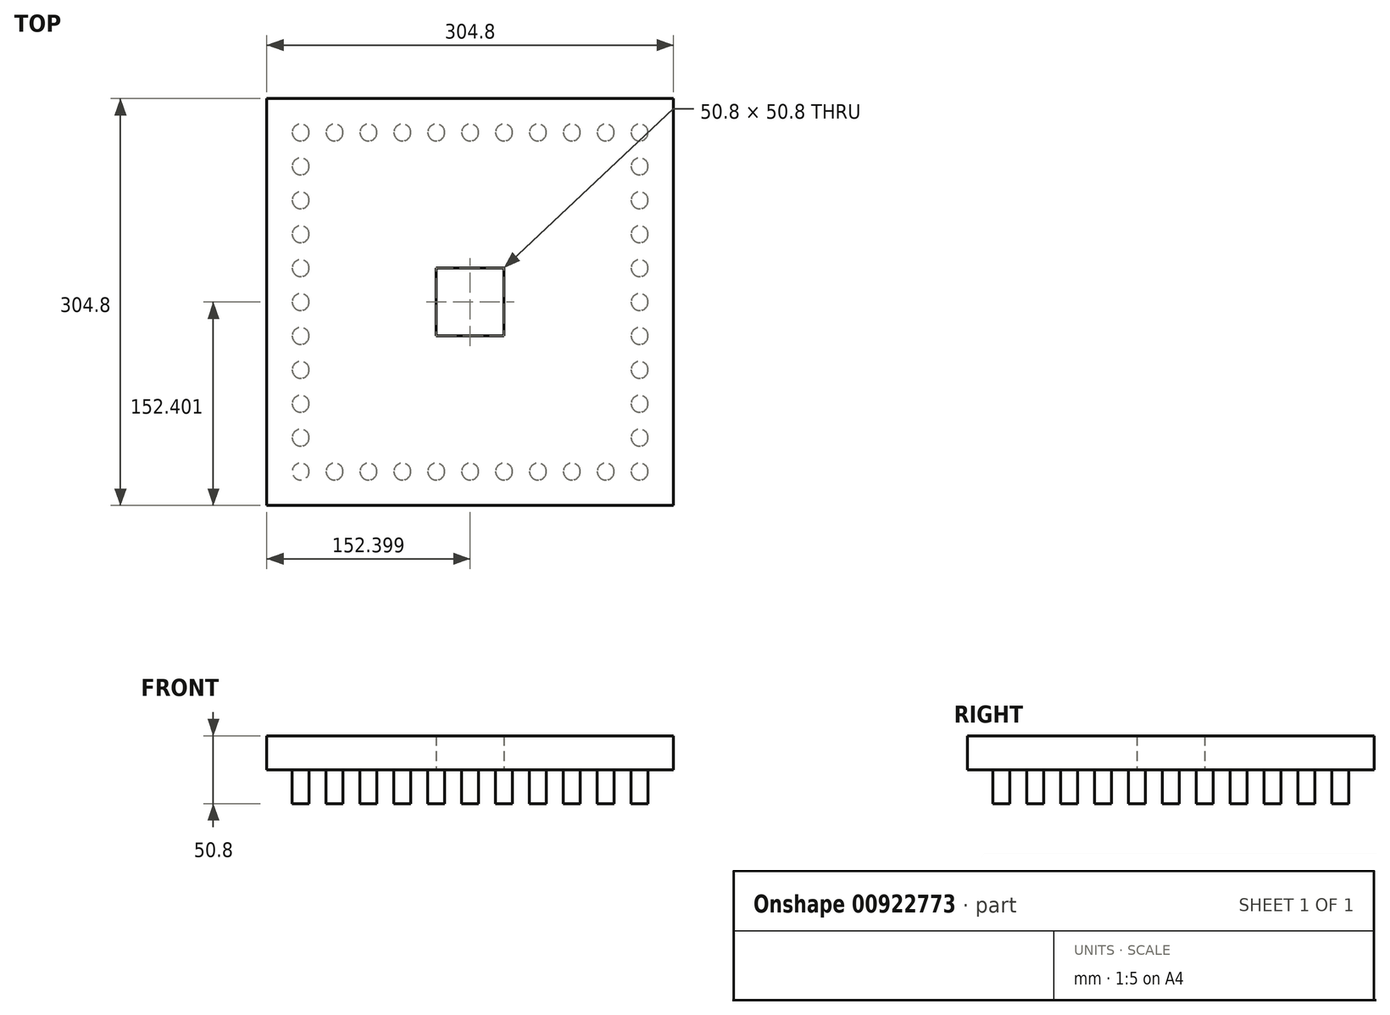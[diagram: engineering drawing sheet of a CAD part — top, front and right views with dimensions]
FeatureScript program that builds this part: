
annotation { "Feature Type Name" : "Feature", "Feature Type Description" : "" }
export const myFeature = defineFeature(function(context is Context, id is Id, definition is map)
    precondition{}
    {
        {
            var Q0;
            Q0=qCreatedBy(makeId("Top.planeOp"),FACE);
            var sketch = newSketch(context, id + "F0", { "sketchPlane" : qUnion([Q0])});
            skLineSegment(sketch, "E0.bottom", {"start": v(-170.88, 244.81) * mm, "end": v(133.92, 244.81) * mm});
            skLineSegment(sketch, "E0.top", {"start": v(-170.88, -59.99) * mm, "end": v(133.92, -59.99) * mm});
            skLineSegment(sketch, "E0.left", {"start": v(-170.88, 244.81) * mm, "end": v(-170.88, -59.99) * mm});
            skLineSegment(sketch, "E0.right", {"start": v(133.92, 244.81) * mm, "end": v(133.92, -59.99) * mm});
            skSolve(sketch);
        }
        {
            var Q0;
            Q0=makeQuery(id+"F0.imprint","IMPRINT",FACE,{"disambiguationData":[TD([[makeQuery(id+"F0.imprint","IMPRINT",EDGE,{"derivedFrom":sQuery(id+"F0.wireOp",EDGE,"E0.bottom")}),-1.0]])]});
            extrude(context, id + "F1", {"entities" : qUnion([Q0]), "depth" : 25.4 * mm, "offsetDistance" : 25.4 * mm});
        }
        {
            var Q0;
            Q0=makeQuery(id+"F1.opExtrude","CAP_FACE",FACE,{"disambiguationData":[OSD([sQuery(id+"F0.wireOp",EDGE,"E0.bottom"),sQuery(id+"F0.wireOp",EDGE,"E0.top"),sQuery(id+"F0.wireOp",EDGE,"E0.left"),sQuery(id+"F0.wireOp",EDGE,"E0.right")])],"isStart":true});
            var sketch = newSketch(context, id + "F2", { "sketchPlane" : qUnion([Q0])});
            skLineSegment(sketch, "E1", {"start": v(-170.88, 59.99) * mm, "end": v(-145.48, 59.99) * mm});
            skLineSegment(sketch, "E2", {"start": v(-145.48, 59.99) * mm, "end": v(-145.48, 34.59) * mm});
            skLineSegment(sketch, "E3", {"start": v(-145.48, 34.59) * mm, "end": v(-145.48, 9.19) * mm});
            skLineSegment(sketch, "E4", {"start": v(-145.48, 9.19) * mm, "end": v(-145.48, -16.21) * mm});
            skLineSegment(sketch, "E5", {"start": v(-145.48, -16.21) * mm, "end": v(-145.48, -41.61) * mm});
            skLineSegment(sketch, "E6", {"start": v(-145.48, -41.61) * mm, "end": v(-145.48, -67.01) * mm});
            skLineSegment(sketch, "E7", {"start": v(-145.48, -67.01) * mm, "end": v(-145.48, -92.41) * mm});
            skLineSegment(sketch, "E8", {"start": v(-145.48, -92.41) * mm, "end": v(-145.48, -117.81) * mm});
            skLineSegment(sketch, "E9", {"start": v(-145.48, -117.81) * mm, "end": v(-145.48, -117.81) * mm});
            skLineSegment(sketch, "E10", {"start": v(-145.48, -117.81) * mm, "end": v(-145.48, -143.21) * mm});
            skLineSegment(sketch, "E11", {"start": v(-145.48, -143.21) * mm, "end": v(-145.48, -168.61) * mm});
            skLineSegment(sketch, "E12", {"start": v(-145.48, -168.61) * mm, "end": v(-145.48, -194.01) * mm});
            skLineSegment(sketch, "E13", {"start": v(-145.48, -194.01) * mm, "end": v(-145.48, -219.41) * mm});
            skLineSegment(sketch, "E14", {"start": v(-145.48, -219.41) * mm, "end": v(-145.48, -244.81) * mm});
            skLineSegment(sketch, "E15", {"start": v(-145.48, -219.41) * mm, "end": v(-120.08, -219.41) * mm});
            skLineSegment(sketch, "E16", {"start": v(-120.08, -219.41) * mm, "end": v(-94.68, -219.41) * mm});
            skLineSegment(sketch, "E17", {"start": v(-94.68, -219.41) * mm, "end": v(-69.28, -219.41) * mm});
            skLineSegment(sketch, "E18", {"start": v(-69.28, -219.41) * mm, "end": v(-43.88, -219.41) * mm});
            skLineSegment(sketch, "E19", {"start": v(-43.88, -219.41) * mm, "end": v(-18.48, -219.41) * mm});
            skLineSegment(sketch, "E20", {"start": v(-18.48, -219.41) * mm, "end": v(6.92, -219.41) * mm});
            skLineSegment(sketch, "E21", {"start": v(6.92, -219.41) * mm, "end": v(32.32, -219.41) * mm});
            skLineSegment(sketch, "E22", {"start": v(32.32, -219.41) * mm, "end": v(57.72, -219.41) * mm});
            skLineSegment(sketch, "E23", {"start": v(57.72, -219.41) * mm, "end": v(83.12, -219.41) * mm});
            skLineSegment(sketch, "E24", {"start": v(83.12, -219.41) * mm, "end": v(108.52, -219.41) * mm});
            skLineSegment(sketch, "E25", {"start": v(108.52, -219.41) * mm, "end": v(108.52, -194.01) * mm});
            skLineSegment(sketch, "E26", {"start": v(108.52, -194.01) * mm, "end": v(108.52, -168.61) * mm});
            skLineSegment(sketch, "E27", {"start": v(108.52, -168.61) * mm, "end": v(108.52, -143.21) * mm});
            skLineSegment(sketch, "E28", {"start": v(108.52, -143.21) * mm, "end": v(108.52, -117.81) * mm});
            skLineSegment(sketch, "E29", {"start": v(108.52, -117.81) * mm, "end": v(108.52, -92.41) * mm});
            skLineSegment(sketch, "E30", {"start": v(108.52, -92.41) * mm, "end": v(108.52, -67.01) * mm});
            skLineSegment(sketch, "E31", {"start": v(108.52, -67.01) * mm, "end": v(108.52, -41.61) * mm});
            skLineSegment(sketch, "E32", {"start": v(108.52, -41.61) * mm, "end": v(108.52, -16.21) * mm});
            skLineSegment(sketch, "E33", {"start": v(108.52, -16.21) * mm, "end": v(108.52, 9.19) * mm});
            skLineSegment(sketch, "E34", {"start": v(108.52, 9.19) * mm, "end": v(108.52, 34.59) * mm});
            skLineSegment(sketch, "E35", {"start": v(108.52, 34.59) * mm, "end": v(83.12, 34.59) * mm});
            skLineSegment(sketch, "E36", {"start": v(83.12, 34.59) * mm, "end": v(57.72, 34.59) * mm});
            skLineSegment(sketch, "E37", {"start": v(57.72, 34.59) * mm, "end": v(32.32, 34.59) * mm});
            skLineSegment(sketch, "E38", {"start": v(32.32, 34.59) * mm, "end": v(6.92, 34.59) * mm});
            skLineSegment(sketch, "E39", {"start": v(6.92, 34.59) * mm, "end": v(-18.48, 34.59) * mm});
            skLineSegment(sketch, "E40", {"start": v(-18.48, 34.59) * mm, "end": v(-43.88, 34.59) * mm});
            skLineSegment(sketch, "E41", {"start": v(-43.88, 34.59) * mm, "end": v(-69.28, 34.59) * mm});
            skLineSegment(sketch, "E42", {"start": v(-69.28, 34.59) * mm, "end": v(-94.68, 34.59) * mm});
            skLineSegment(sketch, "E43", {"start": v(-94.68, 34.59) * mm, "end": v(-120.08, 34.59) * mm});
            skCircle(sketch, "E44", {"center": v(-145.48, 34.59) * mm, "radius": 6.35 * mm});
            skCircle(sketch, "E45", {"center": v(-145.48, 9.19) * mm, "radius": 6.35 * mm});
            skCircle(sketch, "E46", {"center": v(-145.48, -16.21) * mm, "radius": 6.35 * mm});
            skCircle(sketch, "E47", {"center": v(-145.48, -41.61) * mm, "radius": 6.35 * mm});
            skCircle(sketch, "E48", {"center": v(-145.48, -67.01) * mm, "radius": 6.35 * mm});
            skCircle(sketch, "E49", {"center": v(-145.48, -92.41) * mm, "radius": 6.35 * mm});
            skCircle(sketch, "E50", {"center": v(-145.48, -117.81) * mm, "radius": 6.35 * mm});
            skCircle(sketch, "E51", {"center": v(-145.48, -143.21) * mm, "radius": 6.35 * mm});
            skCircle(sketch, "E52", {"center": v(-145.48, -168.61) * mm, "radius": 6.35 * mm});
            skCircle(sketch, "E53", {"center": v(-145.48, -194.01) * mm, "radius": 6.35 * mm});
            skCircle(sketch, "E54", {"center": v(-145.48, -219.41) * mm, "radius": 6.35 * mm});
            skCircle(sketch, "E55", {"center": v(-120.08, -219.41) * mm, "radius": 6.35 * mm});
            skCircle(sketch, "E56", {"center": v(-94.68, -219.41) * mm, "radius": 6.35 * mm});
            skCircle(sketch, "E57", {"center": v(-69.28, -219.41) * mm, "radius": 6.35 * mm});
            skCircle(sketch, "E58", {"center": v(-43.88, -219.41) * mm, "radius": 6.35 * mm});
            skCircle(sketch, "E59", {"center": v(-18.48, -219.41) * mm, "radius": 6.35 * mm});
            skCircle(sketch, "E60", {"center": v(6.92, -219.41) * mm, "radius": 6.35 * mm});
            skCircle(sketch, "E61", {"center": v(32.32, -219.41) * mm, "radius": 6.35 * mm});
            skCircle(sketch, "E62", {"center": v(57.72, -219.41) * mm, "radius": 6.35 * mm});
            skCircle(sketch, "E63", {"center": v(83.12, -219.41) * mm, "radius": 6.35 * mm});
            skCircle(sketch, "E64", {"center": v(108.52, -219.41) * mm, "radius": 6.35 * mm});
            skCircle(sketch, "E65", {"center": v(108.52, -194.01) * mm, "radius": 6.35 * mm});
            skCircle(sketch, "E66", {"center": v(108.52, -168.61) * mm, "radius": 6.35 * mm});
            skCircle(sketch, "E67", {"center": v(108.52, -143.21) * mm, "radius": 6.35 * mm});
            skCircle(sketch, "E68", {"center": v(108.52, -117.81) * mm, "radius": 6.35 * mm});
            skCircle(sketch, "E69", {"center": v(108.52, -92.41) * mm, "radius": 6.35 * mm});
            skCircle(sketch, "E70", {"center": v(108.52, -67.01) * mm, "radius": 6.35 * mm});
            skCircle(sketch, "E71", {"center": v(108.52, -41.61) * mm, "radius": 6.35 * mm});
            skCircle(sketch, "E72", {"center": v(108.52, -16.21) * mm, "radius": 6.35 * mm});
            skCircle(sketch, "E73", {"center": v(108.52, 9.19) * mm, "radius": 6.35 * mm});
            skCircle(sketch, "E74", {"center": v(108.52, 34.59) * mm, "radius": 6.35 * mm});
            skCircle(sketch, "E75", {"center": v(-120.08, 34.59) * mm, "radius": 6.35 * mm});
            skCircle(sketch, "E76", {"center": v(-94.68, 34.59) * mm, "radius": 6.35 * mm});
            skCircle(sketch, "E77", {"center": v(-69.28, 34.59) * mm, "radius": 6.35 * mm});
            skCircle(sketch, "E78", {"center": v(-43.88, 34.59) * mm, "radius": 6.35 * mm});
            skCircle(sketch, "E79", {"center": v(-18.48, 34.59) * mm, "radius": 6.35 * mm});
            skCircle(sketch, "E80", {"center": v(6.92, 34.59) * mm, "radius": 6.35 * mm});
            skCircle(sketch, "E81", {"center": v(32.32, 34.59) * mm, "radius": 6.35 * mm});
            skCircle(sketch, "E82", {"center": v(57.72, 34.59) * mm, "radius": 6.35 * mm});
            skCircle(sketch, "E83", {"center": v(83.12, 34.59) * mm, "radius": 6.35 * mm});
            skSolve(sketch);
        }
        {
            var Q0;
            {var subQ0=sQuery(id+"F2.wireOp",EDGE,"E3");var subQ1=sQuery(id+"F2.wireOp",EDGE,"E2");var subQ2=makeQuery(id+"F2.imprint","INTERSECT",VERTEX,{"derivedFrom":[subQ1,subQ0]});Q0=makeQuery(id+"F2.imprint","IMPRINT",FACE,{"disambiguationData":[TD([[makeQuery(id+"F2.imprint","IMPRINT",EDGE,{"disambiguationData":[TD([[subQ2,1.0]])],"derivedFrom":subQ1}),-1.0]])]});}
            var Q1;
            {var subQ0=sQuery(id+"F2.wireOp",EDGE,"E4");var subQ1=sQuery(id+"F2.wireOp",EDGE,"E3");var subQ2=makeQuery(id+"F2.imprint","INTERSECT",VERTEX,{"derivedFrom":[subQ1,subQ0]});Q1=makeQuery(id+"F2.imprint","IMPRINT",FACE,{"disambiguationData":[TD([[makeQuery(id+"F2.imprint","IMPRINT",EDGE,{"disambiguationData":[TD([[subQ2,1.0]])],"derivedFrom":subQ1}),-1.0]])]});}
            var Q2;
            {var subQ0=sQuery(id+"F2.wireOp",EDGE,"E4");var subQ1=sQuery(id+"F2.wireOp",EDGE,"E3");var subQ2=makeQuery(id+"F2.imprint","INTERSECT",VERTEX,{"derivedFrom":[subQ1,subQ0]});Q2=makeQuery(id+"F2.imprint","IMPRINT",FACE,{"disambiguationData":[TD([[makeQuery(id+"F2.imprint","IMPRINT",EDGE,{"disambiguationData":[TD([[subQ2,1.0]])],"derivedFrom":subQ1}),1.0]])]});}
            var Q3;
            {var subQ0=sQuery(id+"F2.wireOp",EDGE,"E3");var subQ1=sQuery(id+"F2.wireOp",EDGE,"E2");var subQ2=makeQuery(id+"F2.imprint","INTERSECT",VERTEX,{"derivedFrom":[subQ1,subQ0]});Q3=makeQuery(id+"F2.imprint","IMPRINT",FACE,{"disambiguationData":[TD([[makeQuery(id+"F2.imprint","IMPRINT",EDGE,{"disambiguationData":[TD([[subQ2,1.0]])],"derivedFrom":subQ1}),1.0]])]});}
            var Q4;
            {var subQ0=sQuery(id+"F2.wireOp",EDGE,"E5");var subQ1=sQuery(id+"F2.wireOp",EDGE,"E4");var subQ2=makeQuery(id+"F2.imprint","INTERSECT",VERTEX,{"derivedFrom":[subQ1,subQ0]});Q4=makeQuery(id+"F2.imprint","IMPRINT",FACE,{"disambiguationData":[TD([[makeQuery(id+"F2.imprint","IMPRINT",EDGE,{"disambiguationData":[TD([[subQ2,1.0]])],"derivedFrom":subQ1}),-1.0]])]});}
            var Q5;
            {var subQ0=sQuery(id+"F2.wireOp",EDGE,"E5");var subQ1=sQuery(id+"F2.wireOp",EDGE,"E4");var subQ2=makeQuery(id+"F2.imprint","INTERSECT",VERTEX,{"derivedFrom":[subQ1,subQ0]});Q5=makeQuery(id+"F2.imprint","IMPRINT",FACE,{"disambiguationData":[TD([[makeQuery(id+"F2.imprint","IMPRINT",EDGE,{"disambiguationData":[TD([[subQ2,1.0]])],"derivedFrom":subQ1}),1.0]])]});}
            var Q6;
            {var subQ0=sQuery(id+"F2.wireOp",EDGE,"E6");var subQ1=sQuery(id+"F2.wireOp",EDGE,"E5");var subQ2=makeQuery(id+"F2.imprint","INTERSECT",VERTEX,{"derivedFrom":[subQ1,subQ0]});Q6=makeQuery(id+"F2.imprint","IMPRINT",FACE,{"disambiguationData":[TD([[makeQuery(id+"F2.imprint","IMPRINT",EDGE,{"disambiguationData":[TD([[subQ2,1.0]])],"derivedFrom":subQ1}),-1.0]])]});}
            var Q7;
            {var subQ0=sQuery(id+"F2.wireOp",EDGE,"E6");var subQ1=sQuery(id+"F2.wireOp",EDGE,"E5");var subQ2=makeQuery(id+"F2.imprint","INTERSECT",VERTEX,{"derivedFrom":[subQ1,subQ0]});Q7=makeQuery(id+"F2.imprint","IMPRINT",FACE,{"disambiguationData":[TD([[makeQuery(id+"F2.imprint","IMPRINT",EDGE,{"disambiguationData":[TD([[subQ2,1.0]])],"derivedFrom":subQ1}),1.0]])]});}
            var Q8;
            {var subQ0=sQuery(id+"F2.wireOp",EDGE,"E7");var subQ1=sQuery(id+"F2.wireOp",EDGE,"E6");var subQ2=makeQuery(id+"F2.imprint","INTERSECT",VERTEX,{"derivedFrom":[subQ1,subQ0]});Q8=makeQuery(id+"F2.imprint","IMPRINT",FACE,{"disambiguationData":[TD([[makeQuery(id+"F2.imprint","IMPRINT",EDGE,{"disambiguationData":[TD([[subQ2,1.0]])],"derivedFrom":subQ1}),-1.0]])]});}
            var Q9;
            {var subQ0=sQuery(id+"F2.wireOp",EDGE,"E7");var subQ1=sQuery(id+"F2.wireOp",EDGE,"E6");var subQ2=makeQuery(id+"F2.imprint","INTERSECT",VERTEX,{"derivedFrom":[subQ1,subQ0]});Q9=makeQuery(id+"F2.imprint","IMPRINT",FACE,{"disambiguationData":[TD([[makeQuery(id+"F2.imprint","IMPRINT",EDGE,{"disambiguationData":[TD([[subQ2,1.0]])],"derivedFrom":subQ1}),1.0]])]});}
            var Q10;
            {var subQ0=sQuery(id+"F2.wireOp",EDGE,"E8");var subQ1=sQuery(id+"F2.wireOp",EDGE,"E7");var subQ2=makeQuery(id+"F2.imprint","INTERSECT",VERTEX,{"derivedFrom":[subQ1,subQ0]});Q10=makeQuery(id+"F2.imprint","IMPRINT",FACE,{"disambiguationData":[TD([[makeQuery(id+"F2.imprint","IMPRINT",EDGE,{"disambiguationData":[TD([[subQ2,1.0]])],"derivedFrom":subQ1}),1.0]])]});}
            var Q11;
            {var subQ0=sQuery(id+"F2.wireOp",EDGE,"E8");var subQ1=sQuery(id+"F2.wireOp",EDGE,"E7");var subQ2=makeQuery(id+"F2.imprint","INTERSECT",VERTEX,{"derivedFrom":[subQ1,subQ0]});Q11=makeQuery(id+"F2.imprint","IMPRINT",FACE,{"disambiguationData":[TD([[makeQuery(id+"F2.imprint","IMPRINT",EDGE,{"disambiguationData":[TD([[subQ2,1.0]])],"derivedFrom":subQ1}),-1.0]])]});}
            var Q12;
            {var subQ0=sQuery(id+"F2.wireOp",EDGE,"E10");var subQ1=sQuery(id+"F2.wireOp",EDGE,"E8");var subQ2=makeQuery(id+"F2.imprint","INTERSECT",VERTEX,{"derivedFrom":[subQ1,subQ0]});Q12=makeQuery(id+"F2.imprint","IMPRINT",FACE,{"disambiguationData":[TD([[makeQuery(id+"F2.imprint","IMPRINT",EDGE,{"disambiguationData":[TD([[subQ2,1.0]])],"derivedFrom":subQ1}),1.0]])]});}
            var Q13;
            {var subQ0=sQuery(id+"F2.wireOp",EDGE,"E10");var subQ1=sQuery(id+"F2.wireOp",EDGE,"E8");var subQ2=makeQuery(id+"F2.imprint","INTERSECT",VERTEX,{"derivedFrom":[subQ1,subQ0]});Q13=makeQuery(id+"F2.imprint","IMPRINT",FACE,{"disambiguationData":[TD([[makeQuery(id+"F2.imprint","IMPRINT",EDGE,{"disambiguationData":[TD([[subQ2,1.0]])],"derivedFrom":subQ1}),-1.0]])]});}
            var Q14;
            {var subQ0=sQuery(id+"F2.wireOp",EDGE,"E11");var subQ1=sQuery(id+"F2.wireOp",EDGE,"E10");var subQ2=makeQuery(id+"F2.imprint","INTERSECT",VERTEX,{"derivedFrom":[subQ1,subQ0]});Q14=makeQuery(id+"F2.imprint","IMPRINT",FACE,{"disambiguationData":[TD([[makeQuery(id+"F2.imprint","IMPRINT",EDGE,{"disambiguationData":[TD([[subQ2,1.0]])],"derivedFrom":subQ1}),-1.0]])]});}
            var Q15;
            {var subQ0=sQuery(id+"F2.wireOp",EDGE,"E11");var subQ1=sQuery(id+"F2.wireOp",EDGE,"E10");var subQ2=makeQuery(id+"F2.imprint","INTERSECT",VERTEX,{"derivedFrom":[subQ1,subQ0]});Q15=makeQuery(id+"F2.imprint","IMPRINT",FACE,{"disambiguationData":[TD([[makeQuery(id+"F2.imprint","IMPRINT",EDGE,{"disambiguationData":[TD([[subQ2,1.0]])],"derivedFrom":subQ1}),1.0]])]});}
            var Q16;
            Q16=makeQuery(id+"F2.imprint","IMPRINT",FACE,{"disambiguationData":[TD([[makeQuery(id+"F2.imprint","IMPRINT",EDGE,{"derivedFrom":sQuery(id+"F2.wireOp",EDGE,"E75")}),1.0]])]});
            var Q17;
            {var subQ0=sQuery(id+"F2.wireOp",EDGE,"E43");var subQ1=sQuery(id+"F2.wireOp",EDGE,"E42");var subQ2=makeQuery(id+"F2.imprint","INTERSECT",VERTEX,{"derivedFrom":[subQ1,subQ0]});Q17=makeQuery(id+"F2.imprint","IMPRINT",FACE,{"disambiguationData":[TD([[makeQuery(id+"F2.imprint","IMPRINT",EDGE,{"disambiguationData":[TD([[subQ2,1.0]])],"derivedFrom":subQ1}),1.0]])]});}
            var Q18;
            {var subQ0=sQuery(id+"F2.wireOp",EDGE,"E43");var subQ1=sQuery(id+"F2.wireOp",EDGE,"E42");var subQ2=makeQuery(id+"F2.imprint","INTERSECT",VERTEX,{"derivedFrom":[subQ1,subQ0]});Q18=makeQuery(id+"F2.imprint","IMPRINT",FACE,{"disambiguationData":[TD([[makeQuery(id+"F2.imprint","IMPRINT",EDGE,{"disambiguationData":[TD([[subQ2,1.0]])],"derivedFrom":subQ1}),-1.0]])]});}
            var Q19;
            {var subQ0=sQuery(id+"F2.wireOp",EDGE,"E42");var subQ1=sQuery(id+"F2.wireOp",EDGE,"E41");var subQ2=makeQuery(id+"F2.imprint","INTERSECT",VERTEX,{"derivedFrom":[subQ1,subQ0]});Q19=makeQuery(id+"F2.imprint","IMPRINT",FACE,{"disambiguationData":[TD([[makeQuery(id+"F2.imprint","IMPRINT",EDGE,{"disambiguationData":[TD([[subQ2,1.0]])],"derivedFrom":subQ1}),-1.0]])]});}
            var Q20;
            {var subQ0=sQuery(id+"F2.wireOp",EDGE,"E42");var subQ1=sQuery(id+"F2.wireOp",EDGE,"E41");var subQ2=makeQuery(id+"F2.imprint","INTERSECT",VERTEX,{"derivedFrom":[subQ1,subQ0]});Q20=makeQuery(id+"F2.imprint","IMPRINT",FACE,{"disambiguationData":[TD([[makeQuery(id+"F2.imprint","IMPRINT",EDGE,{"disambiguationData":[TD([[subQ2,1.0]])],"derivedFrom":subQ1}),1.0]])]});}
            var Q21;
            {var subQ0=sQuery(id+"F2.wireOp",EDGE,"E41");var subQ1=sQuery(id+"F2.wireOp",EDGE,"E40");var subQ2=makeQuery(id+"F2.imprint","INTERSECT",VERTEX,{"derivedFrom":[subQ1,subQ0]});Q21=makeQuery(id+"F2.imprint","IMPRINT",FACE,{"disambiguationData":[TD([[makeQuery(id+"F2.imprint","IMPRINT",EDGE,{"disambiguationData":[TD([[subQ2,1.0]])],"derivedFrom":subQ1}),-1.0]])]});}
            var Q22;
            {var subQ0=sQuery(id+"F2.wireOp",EDGE,"E41");var subQ1=sQuery(id+"F2.wireOp",EDGE,"E40");var subQ2=makeQuery(id+"F2.imprint","INTERSECT",VERTEX,{"derivedFrom":[subQ1,subQ0]});Q22=makeQuery(id+"F2.imprint","IMPRINT",FACE,{"disambiguationData":[TD([[makeQuery(id+"F2.imprint","IMPRINT",EDGE,{"disambiguationData":[TD([[subQ2,1.0]])],"derivedFrom":subQ1}),1.0]])]});}
            var Q23;
            {var subQ0=sQuery(id+"F2.wireOp",EDGE,"E40");var subQ1=sQuery(id+"F2.wireOp",EDGE,"E39");var subQ2=makeQuery(id+"F2.imprint","INTERSECT",VERTEX,{"derivedFrom":[subQ1,subQ0]});Q23=makeQuery(id+"F2.imprint","IMPRINT",FACE,{"disambiguationData":[TD([[makeQuery(id+"F2.imprint","IMPRINT",EDGE,{"disambiguationData":[TD([[subQ2,1.0]])],"derivedFrom":subQ1}),-1.0]])]});}
            var Q24;
            {var subQ0=sQuery(id+"F2.wireOp",EDGE,"E40");var subQ1=sQuery(id+"F2.wireOp",EDGE,"E39");var subQ2=makeQuery(id+"F2.imprint","INTERSECT",VERTEX,{"derivedFrom":[subQ1,subQ0]});Q24=makeQuery(id+"F2.imprint","IMPRINT",FACE,{"disambiguationData":[TD([[makeQuery(id+"F2.imprint","IMPRINT",EDGE,{"disambiguationData":[TD([[subQ2,1.0]])],"derivedFrom":subQ1}),1.0]])]});}
            var Q25;
            {var subQ0=sQuery(id+"F2.wireOp",EDGE,"E39");var subQ1=sQuery(id+"F2.wireOp",EDGE,"E38");var subQ2=makeQuery(id+"F2.imprint","INTERSECT",VERTEX,{"derivedFrom":[subQ1,subQ0]});Q25=makeQuery(id+"F2.imprint","IMPRINT",FACE,{"disambiguationData":[TD([[makeQuery(id+"F2.imprint","IMPRINT",EDGE,{"disambiguationData":[TD([[subQ2,1.0]])],"derivedFrom":subQ1}),-1.0]])]});}
            var Q26;
            {var subQ0=sQuery(id+"F2.wireOp",EDGE,"E39");var subQ1=sQuery(id+"F2.wireOp",EDGE,"E38");var subQ2=makeQuery(id+"F2.imprint","INTERSECT",VERTEX,{"derivedFrom":[subQ1,subQ0]});Q26=makeQuery(id+"F2.imprint","IMPRINT",FACE,{"disambiguationData":[TD([[makeQuery(id+"F2.imprint","IMPRINT",EDGE,{"disambiguationData":[TD([[subQ2,1.0]])],"derivedFrom":subQ1}),1.0]])]});}
            var Q27;
            {var subQ0=sQuery(id+"F2.wireOp",EDGE,"E38");var subQ1=sQuery(id+"F2.wireOp",EDGE,"E37");var subQ2=makeQuery(id+"F2.imprint","INTERSECT",VERTEX,{"derivedFrom":[subQ1,subQ0]});Q27=makeQuery(id+"F2.imprint","IMPRINT",FACE,{"disambiguationData":[TD([[makeQuery(id+"F2.imprint","IMPRINT",EDGE,{"disambiguationData":[TD([[subQ2,1.0]])],"derivedFrom":subQ1}),-1.0]])]});}
            var Q28;
            {var subQ0=sQuery(id+"F2.wireOp",EDGE,"E38");var subQ1=sQuery(id+"F2.wireOp",EDGE,"E37");var subQ2=makeQuery(id+"F2.imprint","INTERSECT",VERTEX,{"derivedFrom":[subQ1,subQ0]});Q28=makeQuery(id+"F2.imprint","IMPRINT",FACE,{"disambiguationData":[TD([[makeQuery(id+"F2.imprint","IMPRINT",EDGE,{"disambiguationData":[TD([[subQ2,1.0]])],"derivedFrom":subQ1}),1.0]])]});}
            var Q29;
            {var subQ0=sQuery(id+"F2.wireOp",EDGE,"E37");var subQ1=sQuery(id+"F2.wireOp",EDGE,"E36");var subQ2=makeQuery(id+"F2.imprint","INTERSECT",VERTEX,{"derivedFrom":[subQ1,subQ0]});Q29=makeQuery(id+"F2.imprint","IMPRINT",FACE,{"disambiguationData":[TD([[makeQuery(id+"F2.imprint","IMPRINT",EDGE,{"disambiguationData":[TD([[subQ2,1.0]])],"derivedFrom":subQ1}),-1.0]])]});}
            var Q30;
            {var subQ0=sQuery(id+"F2.wireOp",EDGE,"E37");var subQ1=sQuery(id+"F2.wireOp",EDGE,"E36");var subQ2=makeQuery(id+"F2.imprint","INTERSECT",VERTEX,{"derivedFrom":[subQ1,subQ0]});Q30=makeQuery(id+"F2.imprint","IMPRINT",FACE,{"disambiguationData":[TD([[makeQuery(id+"F2.imprint","IMPRINT",EDGE,{"disambiguationData":[TD([[subQ2,1.0]])],"derivedFrom":subQ1}),1.0]])]});}
            var Q31;
            {var subQ0=sQuery(id+"F2.wireOp",EDGE,"E36");var subQ1=sQuery(id+"F2.wireOp",EDGE,"E35");var subQ2=makeQuery(id+"F2.imprint","INTERSECT",VERTEX,{"derivedFrom":[subQ1,subQ0]});Q31=makeQuery(id+"F2.imprint","IMPRINT",FACE,{"disambiguationData":[TD([[makeQuery(id+"F2.imprint","IMPRINT",EDGE,{"disambiguationData":[TD([[subQ2,1.0]])],"derivedFrom":subQ1}),-1.0]])]});}
            var Q32;
            {var subQ0=sQuery(id+"F2.wireOp",EDGE,"E36");var subQ1=sQuery(id+"F2.wireOp",EDGE,"E35");var subQ2=makeQuery(id+"F2.imprint","INTERSECT",VERTEX,{"derivedFrom":[subQ1,subQ0]});Q32=makeQuery(id+"F2.imprint","IMPRINT",FACE,{"disambiguationData":[TD([[makeQuery(id+"F2.imprint","IMPRINT",EDGE,{"disambiguationData":[TD([[subQ2,1.0]])],"derivedFrom":subQ1}),1.0]])]});}
            var Q33;
            {var subQ0=sQuery(id+"F2.wireOp",EDGE,"E35");var subQ1=sQuery(id+"F2.wireOp",EDGE,"E34");var subQ2=makeQuery(id+"F2.imprint","INTERSECT",VERTEX,{"derivedFrom":[subQ1,subQ0]});Q33=makeQuery(id+"F2.imprint","IMPRINT",FACE,{"disambiguationData":[TD([[makeQuery(id+"F2.imprint","IMPRINT",EDGE,{"disambiguationData":[TD([[subQ2,1.0]])],"derivedFrom":subQ1}),-1.0]])]});}
            var Q34;
            {var subQ0=sQuery(id+"F2.wireOp",EDGE,"E35");var subQ1=sQuery(id+"F2.wireOp",EDGE,"E34");var subQ2=makeQuery(id+"F2.imprint","INTERSECT",VERTEX,{"derivedFrom":[subQ1,subQ0]});Q34=makeQuery(id+"F2.imprint","IMPRINT",FACE,{"disambiguationData":[TD([[makeQuery(id+"F2.imprint","IMPRINT",EDGE,{"disambiguationData":[TD([[subQ2,1.0]])],"derivedFrom":subQ1}),1.0]])]});}
            var Q35;
            {var subQ0=sQuery(id+"F2.wireOp",EDGE,"E34");var subQ1=sQuery(id+"F2.wireOp",EDGE,"E33");var subQ2=makeQuery(id+"F2.imprint","INTERSECT",VERTEX,{"derivedFrom":[subQ1,subQ0]});Q35=makeQuery(id+"F2.imprint","IMPRINT",FACE,{"disambiguationData":[TD([[makeQuery(id+"F2.imprint","IMPRINT",EDGE,{"disambiguationData":[TD([[subQ2,1.0]])],"derivedFrom":subQ1}),-1.0]])]});}
            var Q36;
            {var subQ0=sQuery(id+"F2.wireOp",EDGE,"E34");var subQ1=sQuery(id+"F2.wireOp",EDGE,"E33");var subQ2=makeQuery(id+"F2.imprint","INTERSECT",VERTEX,{"derivedFrom":[subQ1,subQ0]});Q36=makeQuery(id+"F2.imprint","IMPRINT",FACE,{"disambiguationData":[TD([[makeQuery(id+"F2.imprint","IMPRINT",EDGE,{"disambiguationData":[TD([[subQ2,1.0]])],"derivedFrom":subQ1}),1.0]])]});}
            var Q37;
            {var subQ0=sQuery(id+"F2.wireOp",EDGE,"E33");var subQ1=sQuery(id+"F2.wireOp",EDGE,"E32");var subQ2=makeQuery(id+"F2.imprint","INTERSECT",VERTEX,{"derivedFrom":[subQ1,subQ0]});Q37=makeQuery(id+"F2.imprint","IMPRINT",FACE,{"disambiguationData":[TD([[makeQuery(id+"F2.imprint","IMPRINT",EDGE,{"disambiguationData":[TD([[subQ2,1.0]])],"derivedFrom":subQ1}),-1.0]])]});}
            var Q38;
            {var subQ0=sQuery(id+"F2.wireOp",EDGE,"E33");var subQ1=sQuery(id+"F2.wireOp",EDGE,"E32");var subQ2=makeQuery(id+"F2.imprint","INTERSECT",VERTEX,{"derivedFrom":[subQ1,subQ0]});Q38=makeQuery(id+"F2.imprint","IMPRINT",FACE,{"disambiguationData":[TD([[makeQuery(id+"F2.imprint","IMPRINT",EDGE,{"disambiguationData":[TD([[subQ2,1.0]])],"derivedFrom":subQ1}),1.0]])]});}
            var Q39;
            {var subQ0=sQuery(id+"F2.wireOp",EDGE,"E32");var subQ1=sQuery(id+"F2.wireOp",EDGE,"E31");var subQ2=makeQuery(id+"F2.imprint","INTERSECT",VERTEX,{"derivedFrom":[subQ1,subQ0]});Q39=makeQuery(id+"F2.imprint","IMPRINT",FACE,{"disambiguationData":[TD([[makeQuery(id+"F2.imprint","IMPRINT",EDGE,{"disambiguationData":[TD([[subQ2,1.0]])],"derivedFrom":subQ1}),-1.0]])]});}
            var Q40;
            {var subQ0=sQuery(id+"F2.wireOp",EDGE,"E32");var subQ1=sQuery(id+"F2.wireOp",EDGE,"E31");var subQ2=makeQuery(id+"F2.imprint","INTERSECT",VERTEX,{"derivedFrom":[subQ1,subQ0]});Q40=makeQuery(id+"F2.imprint","IMPRINT",FACE,{"disambiguationData":[TD([[makeQuery(id+"F2.imprint","IMPRINT",EDGE,{"disambiguationData":[TD([[subQ2,1.0]])],"derivedFrom":subQ1}),1.0]])]});}
            var Q41;
            {var subQ0=sQuery(id+"F2.wireOp",EDGE,"E31");var subQ1=sQuery(id+"F2.wireOp",EDGE,"E30");var subQ2=makeQuery(id+"F2.imprint","INTERSECT",VERTEX,{"derivedFrom":[subQ1,subQ0]});Q41=makeQuery(id+"F2.imprint","IMPRINT",FACE,{"disambiguationData":[TD([[makeQuery(id+"F2.imprint","IMPRINT",EDGE,{"disambiguationData":[TD([[subQ2,1.0]])],"derivedFrom":subQ1}),-1.0]])]});}
            var Q42;
            {var subQ0=sQuery(id+"F2.wireOp",EDGE,"E31");var subQ1=sQuery(id+"F2.wireOp",EDGE,"E30");var subQ2=makeQuery(id+"F2.imprint","INTERSECT",VERTEX,{"derivedFrom":[subQ1,subQ0]});Q42=makeQuery(id+"F2.imprint","IMPRINT",FACE,{"disambiguationData":[TD([[makeQuery(id+"F2.imprint","IMPRINT",EDGE,{"disambiguationData":[TD([[subQ2,1.0]])],"derivedFrom":subQ1}),1.0]])]});}
            var Q43;
            {var subQ0=sQuery(id+"F2.wireOp",EDGE,"E30");var subQ1=sQuery(id+"F2.wireOp",EDGE,"E29");var subQ2=makeQuery(id+"F2.imprint","INTERSECT",VERTEX,{"derivedFrom":[subQ1,subQ0]});Q43=makeQuery(id+"F2.imprint","IMPRINT",FACE,{"disambiguationData":[TD([[makeQuery(id+"F2.imprint","IMPRINT",EDGE,{"disambiguationData":[TD([[subQ2,1.0]])],"derivedFrom":subQ1}),1.0]])]});}
            var Q44;
            {var subQ0=sQuery(id+"F2.wireOp",EDGE,"E30");var subQ1=sQuery(id+"F2.wireOp",EDGE,"E29");var subQ2=makeQuery(id+"F2.imprint","INTERSECT",VERTEX,{"derivedFrom":[subQ1,subQ0]});Q44=makeQuery(id+"F2.imprint","IMPRINT",FACE,{"disambiguationData":[TD([[makeQuery(id+"F2.imprint","IMPRINT",EDGE,{"disambiguationData":[TD([[subQ2,1.0]])],"derivedFrom":subQ1}),-1.0]])]});}
            var Q45;
            {var subQ0=sQuery(id+"F2.wireOp",EDGE,"E29");var subQ1=sQuery(id+"F2.wireOp",EDGE,"E28");var subQ2=makeQuery(id+"F2.imprint","INTERSECT",VERTEX,{"derivedFrom":[subQ1,subQ0]});Q45=makeQuery(id+"F2.imprint","IMPRINT",FACE,{"disambiguationData":[TD([[makeQuery(id+"F2.imprint","IMPRINT",EDGE,{"disambiguationData":[TD([[subQ2,1.0]])],"derivedFrom":subQ1}),-1.0]])]});}
            var Q46;
            {var subQ0=sQuery(id+"F2.wireOp",EDGE,"E29");var subQ1=sQuery(id+"F2.wireOp",EDGE,"E28");var subQ2=makeQuery(id+"F2.imprint","INTERSECT",VERTEX,{"derivedFrom":[subQ1,subQ0]});Q46=makeQuery(id+"F2.imprint","IMPRINT",FACE,{"disambiguationData":[TD([[makeQuery(id+"F2.imprint","IMPRINT",EDGE,{"disambiguationData":[TD([[subQ2,1.0]])],"derivedFrom":subQ1}),1.0]])]});}
            var Q47;
            {var subQ0=sQuery(id+"F2.wireOp",EDGE,"E28");var subQ1=sQuery(id+"F2.wireOp",EDGE,"E27");var subQ2=makeQuery(id+"F2.imprint","INTERSECT",VERTEX,{"derivedFrom":[subQ1,subQ0]});Q47=makeQuery(id+"F2.imprint","IMPRINT",FACE,{"disambiguationData":[TD([[makeQuery(id+"F2.imprint","IMPRINT",EDGE,{"disambiguationData":[TD([[subQ2,1.0]])],"derivedFrom":subQ1}),-1.0]])]});}
            var Q48;
            {var subQ0=sQuery(id+"F2.wireOp",EDGE,"E28");var subQ1=sQuery(id+"F2.wireOp",EDGE,"E27");var subQ2=makeQuery(id+"F2.imprint","INTERSECT",VERTEX,{"derivedFrom":[subQ1,subQ0]});Q48=makeQuery(id+"F2.imprint","IMPRINT",FACE,{"disambiguationData":[TD([[makeQuery(id+"F2.imprint","IMPRINT",EDGE,{"disambiguationData":[TD([[subQ2,1.0]])],"derivedFrom":subQ1}),1.0]])]});}
            var Q49;
            {var subQ0=sQuery(id+"F2.wireOp",EDGE,"E27");var subQ1=sQuery(id+"F2.wireOp",EDGE,"E26");var subQ2=makeQuery(id+"F2.imprint","INTERSECT",VERTEX,{"derivedFrom":[subQ1,subQ0]});Q49=makeQuery(id+"F2.imprint","IMPRINT",FACE,{"disambiguationData":[TD([[makeQuery(id+"F2.imprint","IMPRINT",EDGE,{"disambiguationData":[TD([[subQ2,1.0]])],"derivedFrom":subQ1}),-1.0]])]});}
            var Q50;
            {var subQ0=sQuery(id+"F2.wireOp",EDGE,"E27");var subQ1=sQuery(id+"F2.wireOp",EDGE,"E26");var subQ2=makeQuery(id+"F2.imprint","INTERSECT",VERTEX,{"derivedFrom":[subQ1,subQ0]});Q50=makeQuery(id+"F2.imprint","IMPRINT",FACE,{"disambiguationData":[TD([[makeQuery(id+"F2.imprint","IMPRINT",EDGE,{"disambiguationData":[TD([[subQ2,1.0]])],"derivedFrom":subQ1}),1.0]])]});}
            var Q51;
            {var subQ0=sQuery(id+"F2.wireOp",EDGE,"E26");var subQ1=sQuery(id+"F2.wireOp",EDGE,"E25");var subQ2=makeQuery(id+"F2.imprint","INTERSECT",VERTEX,{"derivedFrom":[subQ1,subQ0]});Q51=makeQuery(id+"F2.imprint","IMPRINT",FACE,{"disambiguationData":[TD([[makeQuery(id+"F2.imprint","IMPRINT",EDGE,{"disambiguationData":[TD([[subQ2,1.0]])],"derivedFrom":subQ1}),-1.0]])]});}
            var Q52;
            {var subQ0=sQuery(id+"F2.wireOp",EDGE,"E26");var subQ1=sQuery(id+"F2.wireOp",EDGE,"E25");var subQ2=makeQuery(id+"F2.imprint","INTERSECT",VERTEX,{"derivedFrom":[subQ1,subQ0]});Q52=makeQuery(id+"F2.imprint","IMPRINT",FACE,{"disambiguationData":[TD([[makeQuery(id+"F2.imprint","IMPRINT",EDGE,{"disambiguationData":[TD([[subQ2,1.0]])],"derivedFrom":subQ1}),1.0]])]});}
            var Q53;
            {var subQ0=sQuery(id+"F2.wireOp",EDGE,"E25");var subQ1=sQuery(id+"F2.wireOp",EDGE,"E24");var subQ2=makeQuery(id+"F2.imprint","INTERSECT",VERTEX,{"derivedFrom":[subQ1,subQ0]});Q53=makeQuery(id+"F2.imprint","IMPRINT",FACE,{"disambiguationData":[TD([[makeQuery(id+"F2.imprint","IMPRINT",EDGE,{"disambiguationData":[TD([[subQ2,1.0]])],"derivedFrom":subQ1}),-1.0]])]});}
            var Q54;
            {var subQ0=sQuery(id+"F2.wireOp",EDGE,"E25");var subQ1=sQuery(id+"F2.wireOp",EDGE,"E24");var subQ2=makeQuery(id+"F2.imprint","INTERSECT",VERTEX,{"derivedFrom":[subQ1,subQ0]});Q54=makeQuery(id+"F2.imprint","IMPRINT",FACE,{"disambiguationData":[TD([[makeQuery(id+"F2.imprint","IMPRINT",EDGE,{"disambiguationData":[TD([[subQ2,1.0]])],"derivedFrom":subQ1}),1.0]])]});}
            var Q55;
            {var subQ0=sQuery(id+"F2.wireOp",EDGE,"E24");var subQ1=sQuery(id+"F2.wireOp",EDGE,"E23");var subQ2=makeQuery(id+"F2.imprint","INTERSECT",VERTEX,{"derivedFrom":[subQ1,subQ0]});Q55=makeQuery(id+"F2.imprint","IMPRINT",FACE,{"disambiguationData":[TD([[makeQuery(id+"F2.imprint","IMPRINT",EDGE,{"disambiguationData":[TD([[subQ2,1.0]])],"derivedFrom":subQ1}),1.0]])]});}
            var Q56;
            {var subQ0=sQuery(id+"F2.wireOp",EDGE,"E24");var subQ1=sQuery(id+"F2.wireOp",EDGE,"E23");var subQ2=makeQuery(id+"F2.imprint","INTERSECT",VERTEX,{"derivedFrom":[subQ1,subQ0]});Q56=makeQuery(id+"F2.imprint","IMPRINT",FACE,{"disambiguationData":[TD([[makeQuery(id+"F2.imprint","IMPRINT",EDGE,{"disambiguationData":[TD([[subQ2,1.0]])],"derivedFrom":subQ1}),-1.0]])]});}
            var Q57;
            {var subQ0=sQuery(id+"F2.wireOp",EDGE,"E23");var subQ1=sQuery(id+"F2.wireOp",EDGE,"E22");var subQ2=makeQuery(id+"F2.imprint","INTERSECT",VERTEX,{"derivedFrom":[subQ1,subQ0]});Q57=makeQuery(id+"F2.imprint","IMPRINT",FACE,{"disambiguationData":[TD([[makeQuery(id+"F2.imprint","IMPRINT",EDGE,{"disambiguationData":[TD([[subQ2,1.0]])],"derivedFrom":subQ1}),1.0]])]});}
            var Q58;
            {var subQ0=sQuery(id+"F2.wireOp",EDGE,"E23");var subQ1=sQuery(id+"F2.wireOp",EDGE,"E22");var subQ2=makeQuery(id+"F2.imprint","INTERSECT",VERTEX,{"derivedFrom":[subQ1,subQ0]});Q58=makeQuery(id+"F2.imprint","IMPRINT",FACE,{"disambiguationData":[TD([[makeQuery(id+"F2.imprint","IMPRINT",EDGE,{"disambiguationData":[TD([[subQ2,1.0]])],"derivedFrom":subQ1}),-1.0]])]});}
            var Q59;
            {var subQ0=sQuery(id+"F2.wireOp",EDGE,"E22");var subQ1=sQuery(id+"F2.wireOp",EDGE,"E21");var subQ2=makeQuery(id+"F2.imprint","INTERSECT",VERTEX,{"derivedFrom":[subQ1,subQ0]});Q59=makeQuery(id+"F2.imprint","IMPRINT",FACE,{"disambiguationData":[TD([[makeQuery(id+"F2.imprint","IMPRINT",EDGE,{"disambiguationData":[TD([[subQ2,1.0]])],"derivedFrom":subQ1}),1.0]])]});}
            var Q60;
            {var subQ0=sQuery(id+"F2.wireOp",EDGE,"E22");var subQ1=sQuery(id+"F2.wireOp",EDGE,"E21");var subQ2=makeQuery(id+"F2.imprint","INTERSECT",VERTEX,{"derivedFrom":[subQ1,subQ0]});Q60=makeQuery(id+"F2.imprint","IMPRINT",FACE,{"disambiguationData":[TD([[makeQuery(id+"F2.imprint","IMPRINT",EDGE,{"disambiguationData":[TD([[subQ2,1.0]])],"derivedFrom":subQ1}),-1.0]])]});}
            var Q61;
            {var subQ0=sQuery(id+"F2.wireOp",EDGE,"E21");var subQ1=sQuery(id+"F2.wireOp",EDGE,"E20");var subQ2=makeQuery(id+"F2.imprint","INTERSECT",VERTEX,{"derivedFrom":[subQ1,subQ0]});Q61=makeQuery(id+"F2.imprint","IMPRINT",FACE,{"disambiguationData":[TD([[makeQuery(id+"F2.imprint","IMPRINT",EDGE,{"disambiguationData":[TD([[subQ2,1.0]])],"derivedFrom":subQ1}),1.0]])]});}
            var Q62;
            {var subQ0=sQuery(id+"F2.wireOp",EDGE,"E21");var subQ1=sQuery(id+"F2.wireOp",EDGE,"E20");var subQ2=makeQuery(id+"F2.imprint","INTERSECT",VERTEX,{"derivedFrom":[subQ1,subQ0]});Q62=makeQuery(id+"F2.imprint","IMPRINT",FACE,{"disambiguationData":[TD([[makeQuery(id+"F2.imprint","IMPRINT",EDGE,{"disambiguationData":[TD([[subQ2,1.0]])],"derivedFrom":subQ1}),-1.0]])]});}
            var Q63;
            {var subQ0=sQuery(id+"F2.wireOp",EDGE,"E20");var subQ1=sQuery(id+"F2.wireOp",EDGE,"E19");var subQ2=makeQuery(id+"F2.imprint","INTERSECT",VERTEX,{"derivedFrom":[subQ1,subQ0]});Q63=makeQuery(id+"F2.imprint","IMPRINT",FACE,{"disambiguationData":[TD([[makeQuery(id+"F2.imprint","IMPRINT",EDGE,{"disambiguationData":[TD([[subQ2,1.0]])],"derivedFrom":subQ1}),1.0]])]});}
            var Q64;
            {var subQ0=sQuery(id+"F2.wireOp",EDGE,"E20");var subQ1=sQuery(id+"F2.wireOp",EDGE,"E19");var subQ2=makeQuery(id+"F2.imprint","INTERSECT",VERTEX,{"derivedFrom":[subQ1,subQ0]});Q64=makeQuery(id+"F2.imprint","IMPRINT",FACE,{"disambiguationData":[TD([[makeQuery(id+"F2.imprint","IMPRINT",EDGE,{"disambiguationData":[TD([[subQ2,1.0]])],"derivedFrom":subQ1}),-1.0]])]});}
            var Q65;
            {var subQ0=sQuery(id+"F2.wireOp",EDGE,"E19");var subQ1=sQuery(id+"F2.wireOp",EDGE,"E18");var subQ2=makeQuery(id+"F2.imprint","INTERSECT",VERTEX,{"derivedFrom":[subQ1,subQ0]});Q65=makeQuery(id+"F2.imprint","IMPRINT",FACE,{"disambiguationData":[TD([[makeQuery(id+"F2.imprint","IMPRINT",EDGE,{"disambiguationData":[TD([[subQ2,1.0]])],"derivedFrom":subQ1}),1.0]])]});}
            var Q66;
            {var subQ0=sQuery(id+"F2.wireOp",EDGE,"E19");var subQ1=sQuery(id+"F2.wireOp",EDGE,"E18");var subQ2=makeQuery(id+"F2.imprint","INTERSECT",VERTEX,{"derivedFrom":[subQ1,subQ0]});Q66=makeQuery(id+"F2.imprint","IMPRINT",FACE,{"disambiguationData":[TD([[makeQuery(id+"F2.imprint","IMPRINT",EDGE,{"disambiguationData":[TD([[subQ2,1.0]])],"derivedFrom":subQ1}),-1.0]])]});}
            var Q67;
            {var subQ0=sQuery(id+"F2.wireOp",EDGE,"E18");var subQ1=sQuery(id+"F2.wireOp",EDGE,"E17");var subQ2=makeQuery(id+"F2.imprint","INTERSECT",VERTEX,{"derivedFrom":[subQ1,subQ0]});Q67=makeQuery(id+"F2.imprint","IMPRINT",FACE,{"disambiguationData":[TD([[makeQuery(id+"F2.imprint","IMPRINT",EDGE,{"disambiguationData":[TD([[subQ2,1.0]])],"derivedFrom":subQ1}),1.0]])]});}
            var Q68;
            {var subQ0=sQuery(id+"F2.wireOp",EDGE,"E18");var subQ1=sQuery(id+"F2.wireOp",EDGE,"E17");var subQ2=makeQuery(id+"F2.imprint","INTERSECT",VERTEX,{"derivedFrom":[subQ1,subQ0]});Q68=makeQuery(id+"F2.imprint","IMPRINT",FACE,{"disambiguationData":[TD([[makeQuery(id+"F2.imprint","IMPRINT",EDGE,{"disambiguationData":[TD([[subQ2,1.0]])],"derivedFrom":subQ1}),-1.0]])]});}
            var Q69;
            {var subQ0=sQuery(id+"F2.wireOp",EDGE,"E17");var subQ1=sQuery(id+"F2.wireOp",EDGE,"E16");var subQ2=makeQuery(id+"F2.imprint","INTERSECT",VERTEX,{"derivedFrom":[subQ1,subQ0]});Q69=makeQuery(id+"F2.imprint","IMPRINT",FACE,{"disambiguationData":[TD([[makeQuery(id+"F2.imprint","IMPRINT",EDGE,{"disambiguationData":[TD([[subQ2,1.0]])],"derivedFrom":subQ1}),1.0]])]});}
            var Q70;
            {var subQ0=sQuery(id+"F2.wireOp",EDGE,"E17");var subQ1=sQuery(id+"F2.wireOp",EDGE,"E16");var subQ2=makeQuery(id+"F2.imprint","INTERSECT",VERTEX,{"derivedFrom":[subQ1,subQ0]});Q70=makeQuery(id+"F2.imprint","IMPRINT",FACE,{"disambiguationData":[TD([[makeQuery(id+"F2.imprint","IMPRINT",EDGE,{"disambiguationData":[TD([[subQ2,1.0]])],"derivedFrom":subQ1}),-1.0]])]});}
            var Q71;
            {var subQ0=sQuery(id+"F2.wireOp",EDGE,"E16");var subQ1=sQuery(id+"F2.wireOp",EDGE,"E15");var subQ2=makeQuery(id+"F2.imprint","INTERSECT",VERTEX,{"derivedFrom":[subQ1,subQ0]});Q71=makeQuery(id+"F2.imprint","IMPRINT",FACE,{"disambiguationData":[TD([[makeQuery(id+"F2.imprint","IMPRINT",EDGE,{"disambiguationData":[TD([[subQ2,1.0]])],"derivedFrom":subQ1}),1.0]])]});}
            var Q72;
            {var subQ0=sQuery(id+"F2.wireOp",EDGE,"E16");var subQ1=sQuery(id+"F2.wireOp",EDGE,"E15");var subQ2=makeQuery(id+"F2.imprint","INTERSECT",VERTEX,{"derivedFrom":[subQ1,subQ0]});Q72=makeQuery(id+"F2.imprint","IMPRINT",FACE,{"disambiguationData":[TD([[makeQuery(id+"F2.imprint","IMPRINT",EDGE,{"disambiguationData":[TD([[subQ2,1.0]])],"derivedFrom":subQ1}),-1.0]])]});}
            var Q73;
            {var subQ0=sQuery(id+"F2.wireOp",EDGE,"E15");var subQ3=sQuery(id+"F2.wireOp",EDGE,"E54");var subQ5=makeQuery(id+"F2.imprint","INTERSECT",VERTEX,{"derivedFrom":[subQ0,subQ3]});Q73=makeQuery(id+"F2.imprint","IMPRINT",FACE,{"disambiguationData":[TD([[makeQuery(id+"F2.imprint","IMPRINT",EDGE,{"disambiguationData":[TD([[subQ5,1.0]])],"derivedFrom":subQ3}),1.0]])]});}
            var Q74;
            {var subQ1=sQuery(id+"F2.wireOp",EDGE,"E13");var subQ3=sQuery(id+"F2.wireOp",EDGE,"E54");var subQ4=makeQuery(id+"F2.imprint","INTERSECT",VERTEX,{"derivedFrom":[subQ1,subQ3]});Q74=makeQuery(id+"F2.imprint","IMPRINT",FACE,{"disambiguationData":[TD([[makeQuery(id+"F2.imprint","IMPRINT",EDGE,{"disambiguationData":[TD([[subQ4,-1.0]])],"derivedFrom":subQ3}),1.0]])]});}
            var Q75;
            {var subQ0=sQuery(id+"F2.wireOp",EDGE,"E15");var subQ3=sQuery(id+"F2.wireOp",EDGE,"E54");var subQ5=makeQuery(id+"F2.imprint","INTERSECT",VERTEX,{"derivedFrom":[subQ0,subQ3]});Q75=makeQuery(id+"F2.imprint","IMPRINT",FACE,{"disambiguationData":[TD([[makeQuery(id+"F2.imprint","IMPRINT",EDGE,{"disambiguationData":[TD([[subQ5,-1.0]])],"derivedFrom":subQ3}),1.0]])]});}
            var Q76;
            {var subQ0=sQuery(id+"F2.wireOp",EDGE,"E13");var subQ1=sQuery(id+"F2.wireOp",EDGE,"E12");var subQ2=makeQuery(id+"F2.imprint","INTERSECT",VERTEX,{"derivedFrom":[subQ1,subQ0]});Q76=makeQuery(id+"F2.imprint","IMPRINT",FACE,{"disambiguationData":[TD([[makeQuery(id+"F2.imprint","IMPRINT",EDGE,{"disambiguationData":[TD([[subQ2,1.0]])],"derivedFrom":subQ1}),1.0]])]});}
            var Q77;
            {var subQ0=sQuery(id+"F2.wireOp",EDGE,"E13");var subQ1=sQuery(id+"F2.wireOp",EDGE,"E12");var subQ2=makeQuery(id+"F2.imprint","INTERSECT",VERTEX,{"derivedFrom":[subQ1,subQ0]});Q77=makeQuery(id+"F2.imprint","IMPRINT",FACE,{"disambiguationData":[TD([[makeQuery(id+"F2.imprint","IMPRINT",EDGE,{"disambiguationData":[TD([[subQ2,1.0]])],"derivedFrom":subQ1}),-1.0]])]});}
            var Q78;
            {var subQ0=sQuery(id+"F2.wireOp",EDGE,"E12");var subQ1=sQuery(id+"F2.wireOp",EDGE,"E11");var subQ2=makeQuery(id+"F2.imprint","INTERSECT",VERTEX,{"derivedFrom":[subQ1,subQ0]});Q78=makeQuery(id+"F2.imprint","IMPRINT",FACE,{"disambiguationData":[TD([[makeQuery(id+"F2.imprint","IMPRINT",EDGE,{"disambiguationData":[TD([[subQ2,1.0]])],"derivedFrom":subQ1}),1.0]])]});}
            var Q79;
            {var subQ0=sQuery(id+"F2.wireOp",EDGE,"E12");var subQ1=sQuery(id+"F2.wireOp",EDGE,"E11");var subQ2=makeQuery(id+"F2.imprint","INTERSECT",VERTEX,{"derivedFrom":[subQ1,subQ0]});Q79=makeQuery(id+"F2.imprint","IMPRINT",FACE,{"disambiguationData":[TD([[makeQuery(id+"F2.imprint","IMPRINT",EDGE,{"disambiguationData":[TD([[subQ2,1.0]])],"derivedFrom":subQ1}),-1.0]])]});}
            extrude(context, id + "F3", {"entities" : qUnion([Q0, Q1, Q2, Q3, Q4, Q5, Q6, Q7, Q8, Q9, Q10, Q11, Q12, Q13, Q14, Q15, Q16, Q17, Q18, Q19, Q20, Q21, Q22, Q23, Q24, Q25, Q26, Q27, Q28, Q29, Q30, Q31, Q32, Q33, Q34, Q35, Q36, Q37, Q38, Q39, Q40, Q41, Q42, Q43, Q44, Q45, Q46, Q47, Q48, Q49, Q50, Q51, Q52, Q53, Q54, Q55, Q56, Q57, Q58, Q59, Q60, Q61, Q62, Q63, Q64, Q65, Q66, Q67, Q68, Q69, Q70, Q71, Q72, Q73, Q74, Q75, Q76, Q77, Q78, Q79]), "operationType" : NewBodyOperationType.ADD, "depth" : 25.4 * mm, "offsetDistance" : 25.4 * mm});
        }
        {
            var Q0;
            Q0=makeQuery(id+"F1.opExtrude","CAP_FACE",FACE,{"disambiguationData":[OSD([sQuery(id+"F0.wireOp",EDGE,"E0.bottom"),sQuery(id+"F0.wireOp",EDGE,"E0.top"),sQuery(id+"F0.wireOp",EDGE,"E0.left"),sQuery(id+"F0.wireOp",EDGE,"E0.right")])],"isStart":true});
            var sketch = newSketch(context, id + "F4", { "sketchPlane" : qUnion([Q0])});
            skLineSegment(sketch, "E84", {"start": v(-170.88, 59.99) * mm, "end": v(-18.48, 59.99) * mm});
            skLineSegment(sketch, "E85", {"start": v(-18.48, 59.99) * mm, "end": v(-18.48, -92.41) * mm});
            skLineSegment(sketch, "E86.bottom", {"start": v(6.92, -67.01) * mm, "end": v(-43.88, -67.01) * mm});
            skLineSegment(sketch, "E86.top", {"start": v(6.92, -117.81) * mm, "end": v(-43.88, -117.81) * mm});
            skLineSegment(sketch, "E86.left", {"start": v(6.92, -67.01) * mm, "end": v(6.92, -117.81) * mm});
            skLineSegment(sketch, "E86.right", {"start": v(-43.88, -67.01) * mm, "end": v(-43.88, -117.81) * mm});
            skPoint(sketch, "E86.middle", {"position": v(-18.48, -92.41) * mm});
            skSolve(sketch);
        }
        {
            var Q0;
            Q0=makeQuery(id+"F4.imprint","IMPRINT",FACE,{"disambiguationData":[TD([[makeQuery(id+"F4.imprint","IMPRINT",EDGE,{"derivedFrom":sQuery(id+"F4.wireOp",EDGE,"E86.top")}),-1.0]])]});
            extrude(context, id + "F5", {"entities" : qUnion([Q0]), "operationType" : NewBodyOperationType.REMOVE, "oppositeDirection" : true, "depth" : 25.4 * mm, "offsetDistance" : 25.4 * mm});
        }
    });
